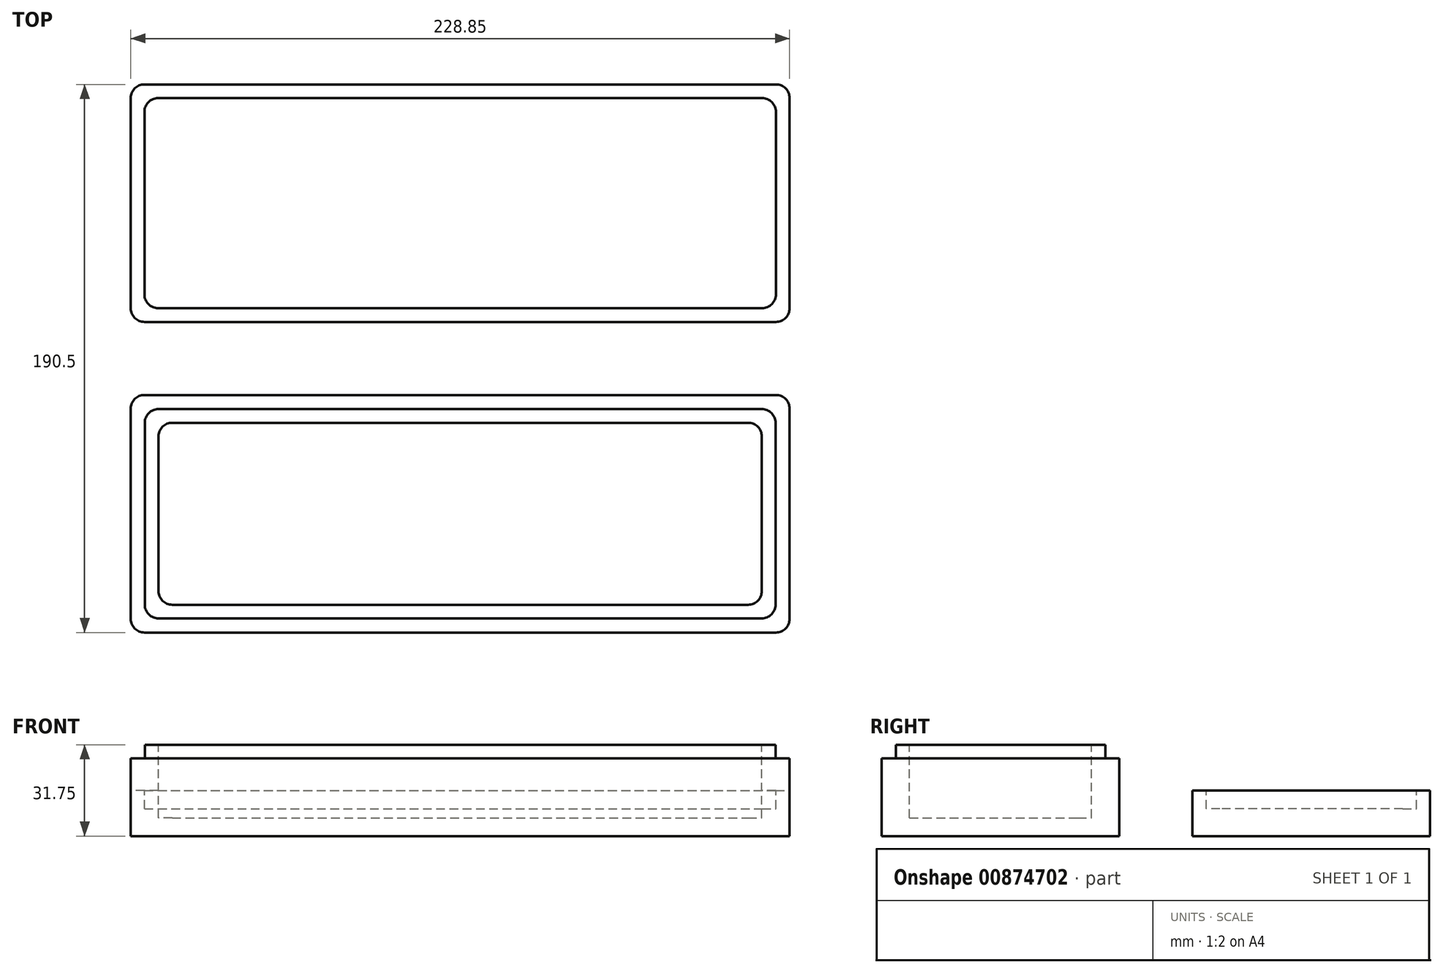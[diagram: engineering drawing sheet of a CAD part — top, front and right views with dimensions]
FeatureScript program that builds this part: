
annotation { "Feature Type Name" : "Feature", "Feature Type Description" : "" }
export const myFeature = defineFeature(function(context is Context, id is Id, definition is map)
    precondition{}
    {
        {
            var Q0;
            Q0=qCreatedBy(makeId("Top.planeOp"),FACE);
            var sketch = newSketch(context, id + "F0", { "sketchPlane" : qUnion([Q0])});
            skLineSegment(sketch, "E0.bottom", {"start": v(0, 0) * mm, "end": v(228.85, 0) * mm});
            skLineSegment(sketch, "E0.top", {"start": v(0, 82.55) * mm, "end": v(228.85, 82.55) * mm});
            skLineSegment(sketch, "E0.left", {"start": v(0, 0) * mm, "end": v(0, 82.55) * mm});
            skLineSegment(sketch, "E0.right", {"start": v(228.85, 0) * mm, "end": v(228.85, 82.55) * mm});
            skSolve(sketch);
        }
        {
            var Q0;
            Q0 = qSketchRegion(id + "F0", true);
            extrude(context, id + "F1", {"entities" : qUnion([Q0]), "depth" : 31.75 * mm, "offsetDistance" : 25.4 * mm});
        }
        {
            var Q0;
            Q0=makeQuery(id+"F1.opExtrude","CAP_FACE",FACE,{"disambiguationData":[OSD([sQuery(id+"F0.wireOp",EDGE,"E0.bottom"),sQuery(id+"F0.wireOp",EDGE,"E0.top"),sQuery(id+"F0.wireOp",EDGE,"E0.left"),sQuery(id+"F0.wireOp",EDGE,"E0.right")])],"isStart":false});
            var sketch = newSketch(context, id + "F2", { "sketchPlane" : qUnion([Q0])});
            skLineSegment(sketch, "E1.bottom", {"start": v(9.65, 9.65) * mm, "end": v(219.2, 9.65) * mm});
            skLineSegment(sketch, "E1.top", {"start": v(9.65, 72.9) * mm, "end": v(219.2, 72.9) * mm});
            skLineSegment(sketch, "E1.left", {"start": v(9.65, 9.65) * mm, "end": v(9.65, 72.9) * mm});
            skLineSegment(sketch, "E1.right", {"start": v(219.2, 9.65) * mm, "end": v(219.2, 72.9) * mm});
            skSolve(sketch);
        }
        {
            var Q0;
            Q0=makeQuery(id+"F2.imprint","IMPRINT",FACE,{"disambiguationData":[TD([[makeQuery(id+"F2.imprint","IMPRINT",EDGE,{"derivedFrom":sQuery(id+"F2.wireOp",EDGE,"E1.bottom")}),1.0]])]});
            extrude(context, id + "F3", {"entities" : qUnion([Q0]), "operationType" : NewBodyOperationType.REMOVE, "oppositeDirection" : true, "depth" : 25.4 * mm, "offsetDistance" : 25.4 * mm});
        }
        {
            var Q0;
            Q0=makeQuery(id+"F1.opExtrude","CAP_FACE",FACE,{"disambiguationData":[OSD([sQuery(id+"F0.wireOp",EDGE,"E0.bottom"),sQuery(id+"F0.wireOp",EDGE,"E0.top"),sQuery(id+"F0.wireOp",EDGE,"E0.left"),sQuery(id+"F0.wireOp",EDGE,"E0.right")])],"isStart":false});
            var sketch = newSketch(context, id + "F4", { "sketchPlane" : qUnion([Q0])});
            skLineSegment(sketch, "E2.bottom", {"start": v(4.89, 77.66) * mm, "end": v(223.96, 77.66) * mm});
            skLineSegment(sketch, "E2.top", {"start": v(4.89, 4.89) * mm, "end": v(223.96, 4.89) * mm});
            skLineSegment(sketch, "E2.left", {"start": v(4.89, 77.66) * mm, "end": v(4.89, 4.89) * mm});
            skLineSegment(sketch, "E2.right", {"start": v(223.96, 77.66) * mm, "end": v(223.96, 4.89) * mm});
            skLineSegment(sketch, "E3.bottom", {"start": v(0, 82.55) * mm, "end": v(228.85, 82.55) * mm});
            skLineSegment(sketch, "E3.top", {"start": v(0, 0) * mm, "end": v(228.85, 0) * mm});
            skLineSegment(sketch, "E3.left", {"start": v(0, 82.55) * mm, "end": v(0, 0) * mm});
            skLineSegment(sketch, "E3.right", {"start": v(228.85, 82.55) * mm, "end": v(228.85, 0) * mm});
            skSolve(sketch);
        }
        {
            var Q0;
            Q0=makeQuery(id+"F4.imprint","IMPRINT",FACE,{"disambiguationData":[TD([[makeQuery(id+"F4.imprint","IMPRINT",EDGE,{"derivedFrom":sQuery(id+"F4.wireOp",EDGE,"E2.bottom")}),1.0]])]});
            extrude(context, id + "F5", {"entities" : qUnion([Q0]), "operationType" : NewBodyOperationType.REMOVE, "oppositeDirection" : true, "depth" : 4.76 * mm, "offsetDistance" : 25.4 * mm});
        }
        {
            var Q0;
            Q0=qCreatedBy(makeId("Top.planeOp"),FACE);
            var sketch = newSketch(context, id + "F6", { "sketchPlane" : qUnion([Q0])});
            skLineSegment(sketch, "E4.bottom", {"start": v(0, 107.95) * mm, "end": v(228.85, 107.95) * mm});
            skLineSegment(sketch, "E4.top", {"start": v(0, 190.5) * mm, "end": v(228.85, 190.5) * mm});
            skLineSegment(sketch, "E4.left", {"start": v(0, 107.95) * mm, "end": v(0, 190.5) * mm});
            skLineSegment(sketch, "E4.right", {"start": v(228.85, 107.95) * mm, "end": v(228.85, 190.5) * mm});
            skSolve(sketch);
        }
        {
            var Q0;
            Q0=makeQuery(id+"F6.imprint","IMPRINT",FACE,{"disambiguationData":[TD([[makeQuery(id+"F6.imprint","IMPRINT",EDGE,{"derivedFrom":sQuery(id+"F6.wireOp",EDGE,"E4.bottom")}),1.0]])]});
            extrude(context, id + "F7", {"entities" : qUnion([Q0]), "depth" : 15.88 * mm, "offsetDistance" : 25.4 * mm});
        }
        {
            var Q0;
            Q0=makeQuery(id+"F7.opExtrude","CAP_FACE",FACE,{"disambiguationData":[OSD([sQuery(id+"F6.wireOp",EDGE,"E4.bottom"),sQuery(id+"F6.wireOp",EDGE,"E4.top"),sQuery(id+"F6.wireOp",EDGE,"E4.left"),sQuery(id+"F6.wireOp",EDGE,"E4.right")])],"isStart":false});
            var sketch = newSketch(context, id + "F8", { "sketchPlane" : qUnion([Q0])});
            skLineSegment(sketch, "E5.bottom", {"start": v(4.76, 185.74) * mm, "end": v(224.1, 185.74) * mm});
            skLineSegment(sketch, "E5.top", {"start": v(4.76, 112.71) * mm, "end": v(224.1, 112.71) * mm});
            skLineSegment(sketch, "E5.left", {"start": v(4.76, 185.74) * mm, "end": v(4.76, 112.71) * mm});
            skLineSegment(sketch, "E5.right", {"start": v(224.1, 185.74) * mm, "end": v(224.1, 112.71) * mm});
            skSolve(sketch);
        }
        {
            var Q0;
            Q0 = qSketchRegion(id + "F8", true);
            extrude(context, id + "F9", {"entities" : qUnion([Q0]), "operationType" : NewBodyOperationType.REMOVE, "oppositeDirection" : true, "depth" : 6.35 * mm, "offsetDistance" : 25.4 * mm});
        }
        {
            var Q0;
            Q0=makeQuery(id+"F3.boolean.opBoolean","COPY",EDGE,{"derivedFrom":makeQuery(id+"F3.opExtrude","SWEPT_EDGE",EDGE,{"disambiguationData":[OSD([sQuery(id+"F2.wireOp",EDGE,"E1.bottom"),sQuery(id+"F2.wireOp",EDGE,"E1.left")])]})});
            var Q1;
            Q1=makeQuery(id+"F3.boolean.opBoolean","COPY",EDGE,{"derivedFrom":makeQuery(id+"F3.opExtrude","SWEPT_EDGE",EDGE,{"disambiguationData":[OSD([sQuery(id+"F2.wireOp",EDGE,"E1.top"),sQuery(id+"F2.wireOp",EDGE,"E1.left")])]})});
            var Q2;
            Q2=makeQuery(id+"F3.boolean.opBoolean","COPY",EDGE,{"derivedFrom":makeQuery(id+"F3.opExtrude","SWEPT_EDGE",EDGE,{"disambiguationData":[OSD([sQuery(id+"F2.wireOp",EDGE,"E1.top"),sQuery(id+"F2.wireOp",EDGE,"E1.right")])]})});
            var Q3;
            Q3=makeQuery(id+"F3.boolean.opBoolean","COPY",EDGE,{"derivedFrom":makeQuery(id+"F3.opExtrude","SWEPT_EDGE",EDGE,{"disambiguationData":[OSD([sQuery(id+"F2.wireOp",EDGE,"E1.bottom"),sQuery(id+"F2.wireOp",EDGE,"E1.right")])]})});
            var Q4;
            Q4=makeQuery(id+"F1.opExtrude","SWEPT_EDGE",EDGE,{"disambiguationData":[OSD([sQuery(id+"F0.wireOp",EDGE,"E0.bottom"),sQuery(id+"F0.wireOp",EDGE,"E0.left")])]});
            var Q5;
            Q5=makeQuery(id+"F1.opExtrude","SWEPT_EDGE",EDGE,{"disambiguationData":[OSD([sQuery(id+"F0.wireOp",EDGE,"E0.top"),sQuery(id+"F0.wireOp",EDGE,"E0.left")])]});
            var Q6;
            Q6=makeQuery(id+"F1.opExtrude","SWEPT_EDGE",EDGE,{"disambiguationData":[OSD([sQuery(id+"F0.wireOp",EDGE,"E0.bottom"),sQuery(id+"F0.wireOp",EDGE,"E0.right")])]});
            var Q7;
            Q7=makeQuery(id+"F1.opExtrude","SWEPT_EDGE",EDGE,{"disambiguationData":[OSD([sQuery(id+"F0.wireOp",EDGE,"E0.top"),sQuery(id+"F0.wireOp",EDGE,"E0.right")])]});
            var Q8;
            Q8=makeQuery(id+"F5.boolean.opBoolean","COPY",EDGE,{"derivedFrom":makeQuery(id+"F5.opExtrude","SWEPT_EDGE",EDGE,{"disambiguationData":[OSD([sQuery(id+"F4.wireOp",EDGE,"E2.bottom"),sQuery(id+"F4.wireOp",EDGE,"E2.right")])]})});
            var Q9;
            Q9=makeQuery(id+"F5.boolean.opBoolean","COPY",EDGE,{"derivedFrom":makeQuery(id+"F5.opExtrude","SWEPT_EDGE",EDGE,{"disambiguationData":[OSD([sQuery(id+"F4.wireOp",EDGE,"E2.top"),sQuery(id+"F4.wireOp",EDGE,"E2.right")])]})});
            var Q10;
            Q10=makeQuery(id+"F5.boolean.opBoolean","COPY",EDGE,{"derivedFrom":makeQuery(id+"F5.opExtrude","SWEPT_EDGE",EDGE,{"disambiguationData":[OSD([sQuery(id+"F4.wireOp",EDGE,"E2.top"),sQuery(id+"F4.wireOp",EDGE,"E2.left")])]})});
            var Q11;
            Q11=makeQuery(id+"F5.boolean.opBoolean","COPY",EDGE,{"derivedFrom":makeQuery(id+"F5.opExtrude","SWEPT_EDGE",EDGE,{"disambiguationData":[OSD([sQuery(id+"F4.wireOp",EDGE,"E2.bottom"),sQuery(id+"F4.wireOp",EDGE,"E2.left")])]})});
            fillet(context, id + "F10", {"entities" : qUnion([Q0, Q1, Q2, Q3, Q4, Q5, Q6, Q7, Q8, Q9, Q10, Q11]), "radius" : 4.76 * mm, "tangentPropagation" : true, "allowEdgeOverflow" : false});
        }
        {
            var Q0;
            Q0=makeQuery(id+"F9.boolean.opBoolean","COPY",EDGE,{"derivedFrom":makeQuery(id+"F9.opExtrude","SWEPT_EDGE",EDGE,{"disambiguationData":[OSD([sQuery(id+"F8.wireOp",EDGE,"E5.bottom"),sQuery(id+"F8.wireOp",EDGE,"E5.left")])]})});
            var Q1;
            Q1=makeQuery(id+"F9.boolean.opBoolean","COPY",EDGE,{"derivedFrom":makeQuery(id+"F9.opExtrude","SWEPT_EDGE",EDGE,{"disambiguationData":[OSD([sQuery(id+"F8.wireOp",EDGE,"E5.bottom"),sQuery(id+"F8.wireOp",EDGE,"E5.right")])]})});
            var Q2;
            Q2=makeQuery(id+"F9.boolean.opBoolean","COPY",EDGE,{"derivedFrom":makeQuery(id+"F9.opExtrude","SWEPT_EDGE",EDGE,{"disambiguationData":[OSD([sQuery(id+"F8.wireOp",EDGE,"E5.top"),sQuery(id+"F8.wireOp",EDGE,"E5.right")])]})});
            var Q3;
            Q3=makeQuery(id+"F9.boolean.opBoolean","COPY",EDGE,{"derivedFrom":makeQuery(id+"F9.opExtrude","SWEPT_EDGE",EDGE,{"disambiguationData":[OSD([sQuery(id+"F8.wireOp",EDGE,"E5.top"),sQuery(id+"F8.wireOp",EDGE,"E5.left")])]})});
            var Q4;
            Q4=makeQuery(id+"F7.opExtrude","SWEPT_EDGE",EDGE,{"disambiguationData":[OSD([sQuery(id+"F6.wireOp",EDGE,"E4.top"),sQuery(id+"F6.wireOp",EDGE,"E4.right")])]});
            var Q5;
            Q5=makeQuery(id+"F7.opExtrude","SWEPT_EDGE",EDGE,{"disambiguationData":[OSD([sQuery(id+"F6.wireOp",EDGE,"E4.top"),sQuery(id+"F6.wireOp",EDGE,"E4.left")])]});
            var Q6;
            Q6=makeQuery(id+"F7.opExtrude","SWEPT_EDGE",EDGE,{"disambiguationData":[OSD([sQuery(id+"F6.wireOp",EDGE,"E4.bottom"),sQuery(id+"F6.wireOp",EDGE,"E4.left")])]});
            var Q7;
            Q7=makeQuery(id+"F7.opExtrude","SWEPT_EDGE",EDGE,{"disambiguationData":[OSD([sQuery(id+"F6.wireOp",EDGE,"E4.bottom"),sQuery(id+"F6.wireOp",EDGE,"E4.right")])]});
            fillet(context, id + "F11", {"entities" : qUnion([Q0, Q1, Q2, Q3, Q4, Q5, Q6, Q7]), "radius" : 4.76 * mm, "tangentPropagation" : true, "allowEdgeOverflow" : false});
        }
    });
